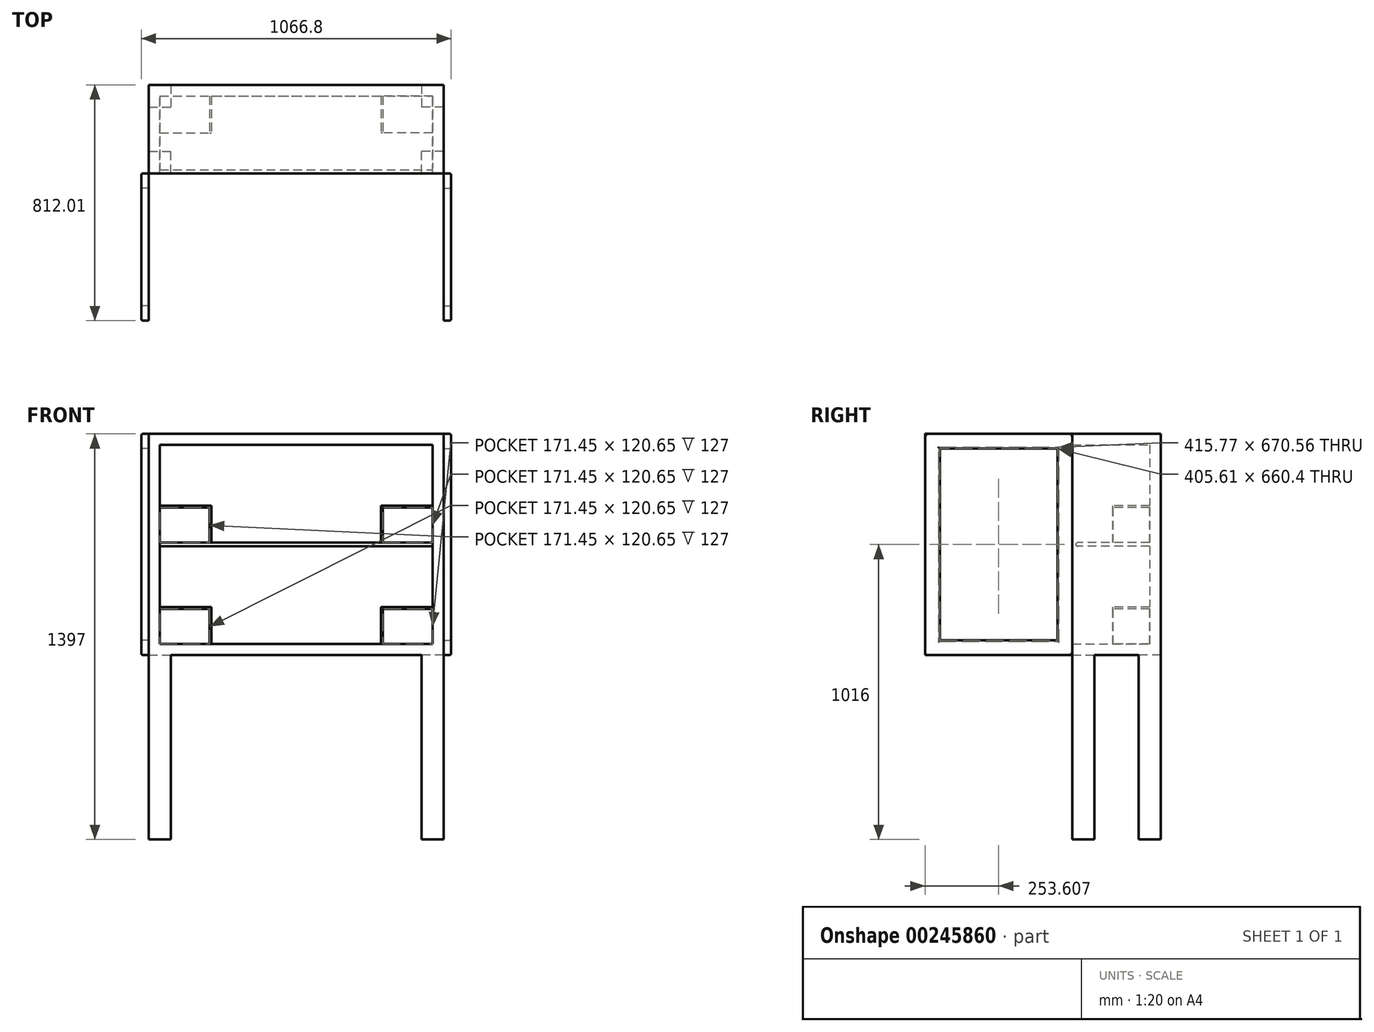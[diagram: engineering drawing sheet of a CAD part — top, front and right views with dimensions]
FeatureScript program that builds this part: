
annotation { "Feature Type Name" : "Feature", "Feature Type Description" : "" }
export const myFeature = defineFeature(function(context is Context, id is Id, definition is map)
    precondition{}
    {
        {
            var Q0;
            Q0=qCreatedBy(makeId("Top.planeOp"),FACE);
            var sketch = newSketch(context, id + "F0", { "sketchPlane" : qUnion([Q0])});
            skLineSegment(sketch, "E0.bottom", {"start": v(508, -152.4) * mm, "end": v(-508, -152.4) * mm});
            skLineSegment(sketch, "E0.top", {"start": v(508, 152.4) * mm, "end": v(-508, 152.4) * mm});
            skLineSegment(sketch, "E0.left", {"start": v(508, -152.4) * mm, "end": v(508, 152.4) * mm});
            skLineSegment(sketch, "E0.right", {"start": v(-508, -152.4) * mm, "end": v(-508, 152.4) * mm});
            skPoint(sketch, "E0.middle", {"position": v(0, 0) * mm});
            skSolve(sketch);
        }
        {
            var Q0;
            Q0=makeQuery(id+"F0.imprint","IMPRINT",FACE,{"disambiguationData":[TD([[makeQuery(id+"F0.imprint","IMPRINT",EDGE,{"derivedFrom":sQuery(id+"F0.wireOp",EDGE,"E0.bottom")}),-1.0]])]});
            extrude(context, id + "F1", {"entities" : qUnion([Q0]), "depth" : 762 * mm});
        }
        {
            var Q0;
            Q0=makeQuery(id+"F1.opExtrude","CAP_FACE",FACE,{"disambiguationData":[OSD([sQuery(id+"F0.wireOp",EDGE,"E0.bottom"),sQuery(id+"F0.wireOp",EDGE,"E0.top"),sQuery(id+"F0.wireOp",EDGE,"E0.left"),sQuery(id+"F0.wireOp",EDGE,"E0.right")])],"isStart":true});
            var sketch = newSketch(context, id + "F2", { "sketchPlane" : qUnion([Q0])});
            skLineSegment(sketch, "E1.bottom", {"start": v(508, 152.4) * mm, "end": v(431.8, 152.4) * mm});
            skLineSegment(sketch, "E1.top", {"start": v(508, 76.2) * mm, "end": v(431.8, 76.2) * mm});
            skLineSegment(sketch, "E1.left", {"start": v(508, 152.4) * mm, "end": v(508, 76.2) * mm});
            skLineSegment(sketch, "E1.right", {"start": v(431.8, 152.4) * mm, "end": v(431.8, 76.2) * mm});
            skLineSegment(sketch, "E2.MirrorCS", {"start": v(-431.8, 152.4) * mm, "end": v(-431.8, 76.2) * mm});
            skLineSegment(sketch, "E3.MirrorCS", {"start": v(-508, 152.4) * mm, "end": v(-431.8, 152.4) * mm});
            skLineSegment(sketch, "E4.MirrorCS", {"start": v(-508, 76.2) * mm, "end": v(-431.8, 76.2) * mm});
            skLineSegment(sketch, "E5.MirrorCS", {"start": v(-508, 152.4) * mm, "end": v(-508, 76.2) * mm});
            skLineSegment(sketch, "E6.MirrorCS", {"start": v(-431.8, -152.4) * mm, "end": v(-431.8, -76.2) * mm});
            skLineSegment(sketch, "E7.MirrorCS", {"start": v(-508, -152.4) * mm, "end": v(-431.8, -152.4) * mm});
            skLineSegment(sketch, "E8.MirrorCS", {"start": v(-508, -152.4) * mm, "end": v(-508, -76.2) * mm});
            skLineSegment(sketch, "E9.MirrorCS", {"start": v(-508, -76.2) * mm, "end": v(-431.8, -76.2) * mm});
            skLineSegment(sketch, "E10.MirrorCS", {"start": v(431.8, -152.4) * mm, "end": v(431.8, -76.2) * mm});
            skLineSegment(sketch, "E11.MirrorCS", {"start": v(508, -76.2) * mm, "end": v(431.8, -76.2) * mm});
            skLineSegment(sketch, "E12.MirrorCS", {"start": v(508, -152.4) * mm, "end": v(431.8, -152.4) * mm});
            skLineSegment(sketch, "E13.MirrorCS", {"start": v(508, -152.4) * mm, "end": v(508, -76.2) * mm});
            skSolve(sketch);
        }
        {
            var Q0;
            Q0=makeQuery(id+"F2.imprint","IMPRINT",FACE,{"disambiguationData":[TD([[makeQuery(id+"F2.imprint","IMPRINT",EDGE,{"derivedFrom":sQuery(id+"F2.wireOp",EDGE,"E1.bottom")}),1.0]])]});
            var Q1;
            Q1=makeQuery(id+"F2.imprint","IMPRINT",FACE,{"disambiguationData":[TD([[makeQuery(id+"F2.imprint","IMPRINT",EDGE,{"derivedFrom":sQuery(id+"F2.wireOp",EDGE,"E10.MirrorCS")}),-1.0]])]});
            var Q2;
            Q2=makeQuery(id+"F2.imprint","IMPRINT",FACE,{"disambiguationData":[TD([[makeQuery(id+"F2.imprint","IMPRINT",EDGE,{"derivedFrom":sQuery(id+"F2.wireOp",EDGE,"E2.MirrorCS")}),-1.0]])]});
            var Q3;
            Q3=makeQuery(id+"F2.imprint","IMPRINT",FACE,{"disambiguationData":[TD([[makeQuery(id+"F2.imprint","IMPRINT",EDGE,{"derivedFrom":sQuery(id+"F2.wireOp",EDGE,"E6.MirrorCS")}),1.0]])]});
            extrude(context, id + "F3", {"entities" : qUnion([Q0, Q1, Q2, Q3]), "operationType" : NewBodyOperationType.ADD, "depth" : 635 * mm});
        }
        {
            var Q0;
            Q0=makeQuery(id+"F3.boolean.opBoolean","MERGE",FACE,{"derivedFrom":[makeQuery(id+"F1.opExtrude","SWEPT_FACE",FACE,{"disambiguationData":[OSD([sQuery(id+"F0.wireOp",EDGE,"E0.bottom")])]}),makeQuery(id+"F3.opExtrude","SWEPT_FACE",FACE,{"disambiguationData":[OSD([sQuery(id+"F2.wireOp",EDGE,"E1.bottom")])]}),makeQuery(id+"F3.opExtrude","SWEPT_FACE",FACE,{"disambiguationData":[OSD([sQuery(id+"F2.wireOp",EDGE,"E3.MirrorCS")])]})]});
            shell(context, id + "F4", {"entities" : qUnion([Q0]), "thickness" : 38.1 * mm});
        }
        {
            var Q0;
            Q0=makeQuery(id+"F4.opShell","OFFSET_FACE",FACE,{"disambiguationData":[OSD([sQuery(id+"F0.wireOp",EDGE,"E0.top"),sQuery(id+"F2.wireOp",EDGE,"E7.MirrorCS"),sQuery(id+"F2.wireOp",EDGE,"E12.MirrorCS")])]});
            var sketch = newSketch(context, id + "F5", { "sketchPlane" : qUnion([Q0])});
            skLineSegment(sketch, "E14", {"start": v(-469.9, 381) * mm, "end": v(469.9, 381) * mm});
            skSolve(sketch);
        }
        {
            var Q0;
            Q0=sQuery(id+"F5.wireOp",EDGE,"E14");
            extrude(context, id + "F6", {"bodyType" : ToolBodyType.SURFACE, "surfaceEntities" : qUnion([Q0]), "depth" : 254 * mm});
        }
        {
            var Q0;
            Q0=makeQuery(id+"F6.opExtrude","SWEPT_FACE",FACE,{"disambiguationData":[OSD([sQuery(id+"F5.wireOp",EDGE,"E14")])]});
            extrude(context, id + "F7", {"entities" : qUnion([Q0]), "operationType" : NewBodyOperationType.ADD, "endBound" : BoundingType.SYMMETRIC, "depth" : 12.7 * mm});
        }
        {
            var Q0;
            {var subQ2=sQuery(id+"F0.wireOp",EDGE,"E0.top");Q0=makeQuery(id+"F7.boolean.opBoolean","SPLIT",FACE,{"disambiguationData":[TD([makeQuery(id+"F7.opExtrude","CAP_FACE",FACE,{"disambiguationData":[OSD([sQuery(id+"F5.wireOp",EDGE,"E14")])],"isStart":true})])],"derivedFrom":makeQuery(id+"F4.opShell","OFFSET_FACE",FACE,{"disambiguationData":[OSD([subQ2,sQuery(id+"F2.wireOp",EDGE,"E7.MirrorCS"),sQuery(id+"F2.wireOp",EDGE,"E12.MirrorCS")])]})});}
            var sketch = newSketch(context, id + "F8", { "sketchPlane" : qUnion([Q0])});
            skLineSegment(sketch, "E15", {"start": v(-469.9, 514.35) * mm, "end": v(-292.1, 514.35) * mm});
            skLineSegment(sketch, "E16", {"start": v(-292.1, 514.35) * mm, "end": v(-292.1, 387.35) * mm});
            skLineSegment(sketch, "E17.MirrorCS", {"start": v(469.9, 514.35) * mm, "end": v(292.1, 514.35) * mm});
            skLineSegment(sketch, "E18.MirrorCS", {"start": v(292.1, 514.35) * mm, "end": v(292.1, 387.35) * mm});
            skSolve(sketch);
        }
        {
            var Q0;
            {var subQ2=sQuery(id+"F0.wireOp",EDGE,"E0.top");Q0=makeQuery(id+"F7.boolean.opBoolean","SPLIT",FACE,{"disambiguationData":[TD([makeQuery(id+"F7.opExtrude","CAP_FACE",FACE,{"disambiguationData":[OSD([sQuery(id+"F5.wireOp",EDGE,"E14")])],"isStart":false})])],"derivedFrom":makeQuery(id+"F4.opShell","OFFSET_FACE",FACE,{"disambiguationData":[OSD([subQ2,sQuery(id+"F2.wireOp",EDGE,"E7.MirrorCS"),sQuery(id+"F2.wireOp",EDGE,"E12.MirrorCS")])]})});}
            var sketch = newSketch(context, id + "F9", { "sketchPlane" : qUnion([Q0])});
            skLineSegment(sketch, "E19", {"start": v(-469.9, 165.1) * mm, "end": v(-292.1, 165.1) * mm});
            skLineSegment(sketch, "E20", {"start": v(-292.1, 165.1) * mm, "end": v(-292.1, 38.1) * mm});
            skLineSegment(sketch, "E21.MirrorCS", {"start": v(469.9, 165.1) * mm, "end": v(292.1, 165.1) * mm});
            skLineSegment(sketch, "E22.MirrorCS", {"start": v(292.1, 165.1) * mm, "end": v(292.1, 38.1) * mm});
            skSolve(sketch);
        }
        {
            var Q0;
            Q0=sQuery(id+"F8.wireOp",EDGE,"E15");
            var Q1;
            Q1=sQuery(id+"F8.wireOp",EDGE,"E16");
            var Q2;
            Q2=sQuery(id+"F8.wireOp",EDGE,"E18.MirrorCS");
            var Q3;
            Q3=sQuery(id+"F8.wireOp",EDGE,"E17.MirrorCS");
            var Q4;
            Q4=sQuery(id+"F9.wireOp",EDGE,"E19");
            var Q5;
            Q5=sQuery(id+"F9.wireOp",EDGE,"E20");
            var Q6;
            Q6=sQuery(id+"F9.wireOp",EDGE,"E22.MirrorCS");
            var Q7;
            Q7=sQuery(id+"F9.wireOp",EDGE,"E21.MirrorCS");
            extrude(context, id + "F10", {"bodyType" : ToolBodyType.SURFACE, "surfaceEntities" : qUnion([Q0, Q1, Q2, Q3, Q4, Q5, Q6, Q7]), "depth" : 127 * mm});
        }
        {
            var Q0;
            Q0=makeQuery(id+"F10.opExtrude","SWEPT_FACE",FACE,{"disambiguationData":[OSD([sQuery(id+"F8.wireOp",EDGE,"E15")])]});
            var Q1;
            Q1=makeQuery(id+"F10.opExtrude","SWEPT_FACE",FACE,{"disambiguationData":[OSD([sQuery(id+"F9.wireOp",EDGE,"E19")])]});
            var Q2;
            Q2=makeQuery(id+"F10.opExtrude","SWEPT_FACE",FACE,{"disambiguationData":[OSD([sQuery(id+"F8.wireOp",EDGE,"E17.MirrorCS")])]});
            var Q3;
            Q3=makeQuery(id+"F10.opExtrude","SWEPT_FACE",FACE,{"disambiguationData":[OSD([sQuery(id+"F9.wireOp",EDGE,"E21.MirrorCS")])]});
            extrude(context, id + "F11", {"entities" : qUnion([Q0, Q1, Q2, Q3]), "operationType" : NewBodyOperationType.ADD, "depth" : 6.35 * mm});
        }
        {
            var Q0;
            Q0=makeQuery(id+"F10.opExtrude","SWEPT_FACE",FACE,{"disambiguationData":[OSD([sQuery(id+"F8.wireOp",EDGE,"E16")])]});
            var Q1;
            Q1=makeQuery(id+"F10.opExtrude","SWEPT_FACE",FACE,{"disambiguationData":[OSD([sQuery(id+"F9.wireOp",EDGE,"E20")])]});
            extrude(context, id + "F12", {"entities" : qUnion([Q0, Q1]), "operationType" : NewBodyOperationType.ADD, "depth" : 6.35 * mm});
        }
        {
            var Q0;
            Q0=makeQuery(id+"F10.opExtrude","SWEPT_FACE",FACE,{"disambiguationData":[OSD([sQuery(id+"F8.wireOp",EDGE,"E18.MirrorCS")])]});
            var Q1;
            Q1=makeQuery(id+"F10.opExtrude","SWEPT_FACE",FACE,{"disambiguationData":[OSD([sQuery(id+"F9.wireOp",EDGE,"E22.MirrorCS")])]});
            extrude(context, id + "F13", {"entities" : qUnion([Q0, Q1]), "operationType" : NewBodyOperationType.ADD, "oppositeDirection" : true, "depth" : 6.35 * mm});
        }
        {
            var Q0;
            Q0=makeQuery(id+"F3.boolean.opBoolean","MERGE",FACE,{"derivedFrom":[makeQuery(id+"F1.opExtrude","SWEPT_FACE",FACE,{"disambiguationData":[OSD([sQuery(id+"F0.wireOp",EDGE,"E0.left")])]}),makeQuery(id+"F3.opExtrude","SWEPT_FACE",FACE,{"disambiguationData":[OSD([sQuery(id+"F2.wireOp",EDGE,"E1.left")])]}),makeQuery(id+"F3.opExtrude","SWEPT_FACE",FACE,{"disambiguationData":[OSD([sQuery(id+"F2.wireOp",EDGE,"E13.MirrorCS")])]})]});
            cPlane(context, id + "F14", {"entities" : qUnion([Q0]), "cplaneType" : CPlaneType.OFFSET, "offset" : 0 * mm, "width" : 152.4 * mm, "height" : 152.4 * mm});
        }
        {
            var Q0;
            Q0=qCreatedBy(id+"F14.planeOp",FACE);
            var sketch = newSketch(context, id + "F15", { "sketchPlane" : qUnion([Q0])});
            skLineSegment(sketch, "E23.bottom", {"start": v(-152.4, 762) * mm, "end": v(-659.6, 762) * mm});
            skLineSegment(sketch, "E23.top", {"start": v(-152.4, 0) * mm, "end": v(-659.6, 0) * mm});
            skLineSegment(sketch, "E23.left", {"start": v(-152.4, 762) * mm, "end": v(-152.4, 0) * mm});
            skLineSegment(sketch, "E23.right", {"start": v(-659.6, 762) * mm, "end": v(-659.6, 0) * mm});
            skSolve(sketch);
        }
        {
            var Q0;
            Q0=makeQuery(id+"F15.imprint","IMPRINT",FACE,{"disambiguationData":[TD([[makeQuery(id+"F15.imprint","IMPRINT",EDGE,{"derivedFrom":sQuery(id+"F15.wireOp",EDGE,"E23.bottom")}),1.0]])]});
            extrude(context, id + "F16", {"entities" : qUnion([Q0]), "depth" : 25.4 * mm});
        }
        {
            var Q0;
            Q0=makeQuery(id+"F16.opExtrude","CAP_FACE",FACE,{"disambiguationData":[OSD([sQuery(id+"F15.wireOp",EDGE,"E23.bottom"),sQuery(id+"F15.wireOp",EDGE,"E23.top"),sQuery(id+"F15.wireOp",EDGE,"E23.left"),sQuery(id+"F15.wireOp",EDGE,"E23.right")])],"isStart":false});
            var sketch = newSketch(context, id + "F17", { "sketchPlane" : qUnion([Q0])});
            skLineSegment(sketch, "E24.bottom", {"start": v(-203.2, 50.8) * mm, "end": v(-608.8, 50.8) * mm});
            skLineSegment(sketch, "E24.top", {"start": v(-203.2, 711.2) * mm, "end": v(-608.8, 711.2) * mm});
            skLineSegment(sketch, "E24.left", {"start": v(-203.2, 50.8) * mm, "end": v(-203.2, 711.2) * mm});
            skLineSegment(sketch, "E24.right", {"start": v(-608.8, 50.8) * mm, "end": v(-608.8, 711.2) * mm});
            skPoint(sketch, "E24.middle", {"position": v(-406, 381) * mm});
            skPoint(sketch, "E24.middle.positionSnap0", {"position": v(-406, 762) * mm});
            skPoint(sketch, "E24.middle.positionSnap1", {"position": v(-659.6, 381) * mm});
            skPoint(sketch, "E24.centerSnap0", {"position": v(-406, 762) * mm});
            skPoint(sketch, "E24.centerSnap1", {"position": v(-659.6, 381) * mm});
            skSolve(sketch);
        }
        {
            var Q0;
            Q0=makeQuery(id+"F17.imprint","IMPRINT",FACE,{"disambiguationData":[TD([[makeQuery(id+"F17.imprint","IMPRINT",EDGE,{"derivedFrom":sQuery(id+"F17.wireOp",EDGE,"E24.bottom")}),-1.0]])]});
            extrude(context, id + "F18", {"entities" : qUnion([Q0]), "operationType" : NewBodyOperationType.REMOVE, "oppositeDirection" : true, "depth" : 25.4 * mm});
        }
        {
            var Q0;
            Q0=makeQuery(id+"F16.opExtrude","CAP_FACE",FACE,{"disambiguationData":[OSD([sQuery(id+"F15.wireOp",EDGE,"E23.bottom"),sQuery(id+"F15.wireOp",EDGE,"E23.top"),sQuery(id+"F15.wireOp",EDGE,"E23.left"),sQuery(id+"F15.wireOp",EDGE,"E23.right")])],"isStart":false});
            fillet(context, id + "F19", {"entities" : qUnion([Q0]), "radius" : 5.08 * mm, "tangentPropagation" : true, "allowEdgeOverflow" : false});
        }
        {
            var Q0;
            Q0=makeQuery(id+"F16.opExtrude","SWEPT_BODY",BODY,{"disambiguationData":[OSD([sQuery(id+"F15.wireOp",EDGE,"E23.bottom"),sQuery(id+"F15.wireOp",EDGE,"E23.top"),sQuery(id+"F15.wireOp",EDGE,"E23.left"),sQuery(id+"F15.wireOp",EDGE,"E23.right")])]});
            var Q1;
            Q1=qCreatedBy(makeId("Right.planeOp"),FACE);
            mirror(context, id + "F20", {"entities" : qUnion([Q0]), "mirrorPlane" : qUnion([Q1])});
        }
        {
            var Q0;
            {var subQ0=sQuery(id+"F5.wireOp",EDGE,"E14");Q0=makeQuery(id+"F7.opExtrude","CAP_EDGE",EDGE,{"disambiguationData":[OSD([subQ0]),TDD([makeQuery(id+"F6.opExtrude","CAP_EDGE",EDGE,{"disambiguationData":[OSD([subQ0])],"isStart":false})])],"isStart":true});}
            var Q1;
            {var subQ0=sQuery(id+"F5.wireOp",EDGE,"E14");Q1=makeQuery(id+"F7.opExtrude","CAP_EDGE",EDGE,{"disambiguationData":[OSD([subQ0]),TDD([makeQuery(id+"F6.opExtrude","CAP_EDGE",EDGE,{"disambiguationData":[OSD([subQ0])],"isStart":false})])],"isStart":false});}
            fillet(context, id + "F21", {"entities" : qUnion([Q0, Q1]), "radius" : 5.08 * mm, "tangentPropagation" : true, "allowEdgeOverflow" : false});
        }
    });
